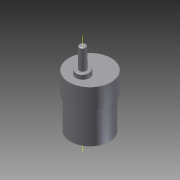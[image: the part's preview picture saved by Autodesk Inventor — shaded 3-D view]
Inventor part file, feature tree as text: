
AUTODESK INVENTOR PART (.ipt)
format: ipt  version: 2012 (Build 160160000, 160)  size: 233,472 bytes
history: native  units: mm
features: extrude x10, sketch x10, projected_geometry x7, fillet x5, other x1
ambient origin geometry x8: Origin, YZ Plane, XZ Plane, XY Plane, X Axis, Y Axis, Z Axis, Center Point
bodies: Solid1 (feature_tree)
feature tree (33):
  extrude  "Extrusion1"  Depth=28.77mm TaperAngle=0.0deg
  extrude  "Extrusion2"  Depth=18.0mm TaperAngle=0.0deg
  extrude  "Extrusion3"  Depth=31.3mm
  fillet  "Fillet1"  Radius=6.0mm
  extrude  "Extrusion4"  Depth=37.7mm
  extrude  "Extrusion5"  TaperAngle=0.0deg  [1 undecoded]
  extrude  "Extrusion6"  Depth=0.5mm
  extrude  "Extrusion7"  Depth=18.2mm TaperAngle=0.0deg
  fillet  "Fillet2"  Radius=5.45mm
  fillet  "Fillet3"  Radius=12.1mm
  extrude  "Extrusion8"  Depth=0.5mm TaperAngle=0.0deg
  extrude  "Extrusion9"  Depth=3.3mm TaperAngle=0.0deg
  fillet  "Fillet4"  Radius=3.0mm
  extrude  "Extrusion10"  Depth=2.0mm
  fillet  "Fillet5"  Radius=1.0mm
  other  "Work Axis1"
  sketch  "Sketch1"  dims[d0=34.9mm d1=28.77mm d2=0.0mm]
  sketch  "Sketch2"  dims[d3=37.7mm d4=18.0mm d5=0.0mm]
  sketch  "Sketch3"  dims[d6=12.0mm d7=31.3mm d8=6.0mm]
  projected_geometry  "Projected Loop1"
  sketch  "Sketch4"  dims[d9=6.0mm d10=37.7mm]
  sketch  "Sketch5"  dims[d11=37.7mm d12=0.0mm]
  sketch  "Sketch6"  dims[d13=4.1mm d14=0.0mm d15=0.5mm]
  projected_geometry  "Projected Loop2"
  sketch  "Sketch7"  dims[d16=6.0mm d17=18.2mm d18=0.0mm d19=5.45mm d20=12.1mm d21=0.0mm]
  sketch  "Sketch8"  dims[d24=33.5mm d25=0.5mm d26=0.0mm]
  projected_geometry  "Projected Loop3"
  sketch  "Sketch9"  dims[d27=7.9mm d28=3.3mm d29=0.0mm d30=3.0mm]
  projected_geometry  "Projected Loop4"
  projected_geometry  "Projected Loop5"
  sketch  "Sketch10"  dims[d31=3.0mm d32=2.0mm d33=1.0mm d34=0.0mm d35=0.5mm d36=2.85mm d37=12.0mm d40=6.4mm d41=6.4mm d42=9.5mm d43=34.9mm d44=34.9mm d45=34.9mm d46=7.35mm d47=13.2mm d48=6.9mm d49=0.0mm d50=1.0mm d51=1.0mm d52=6.9mm d53=0.0mm d54=0.75mm]
  projected_geometry  "Projected Loop6"
  projected_geometry  "Projected Loop7"
note: 1 required parameter value undecoded (feature->parameter linkage not recoverable at this tier; creation-order binding heuristic only, values carry confidence <= 0.55)
